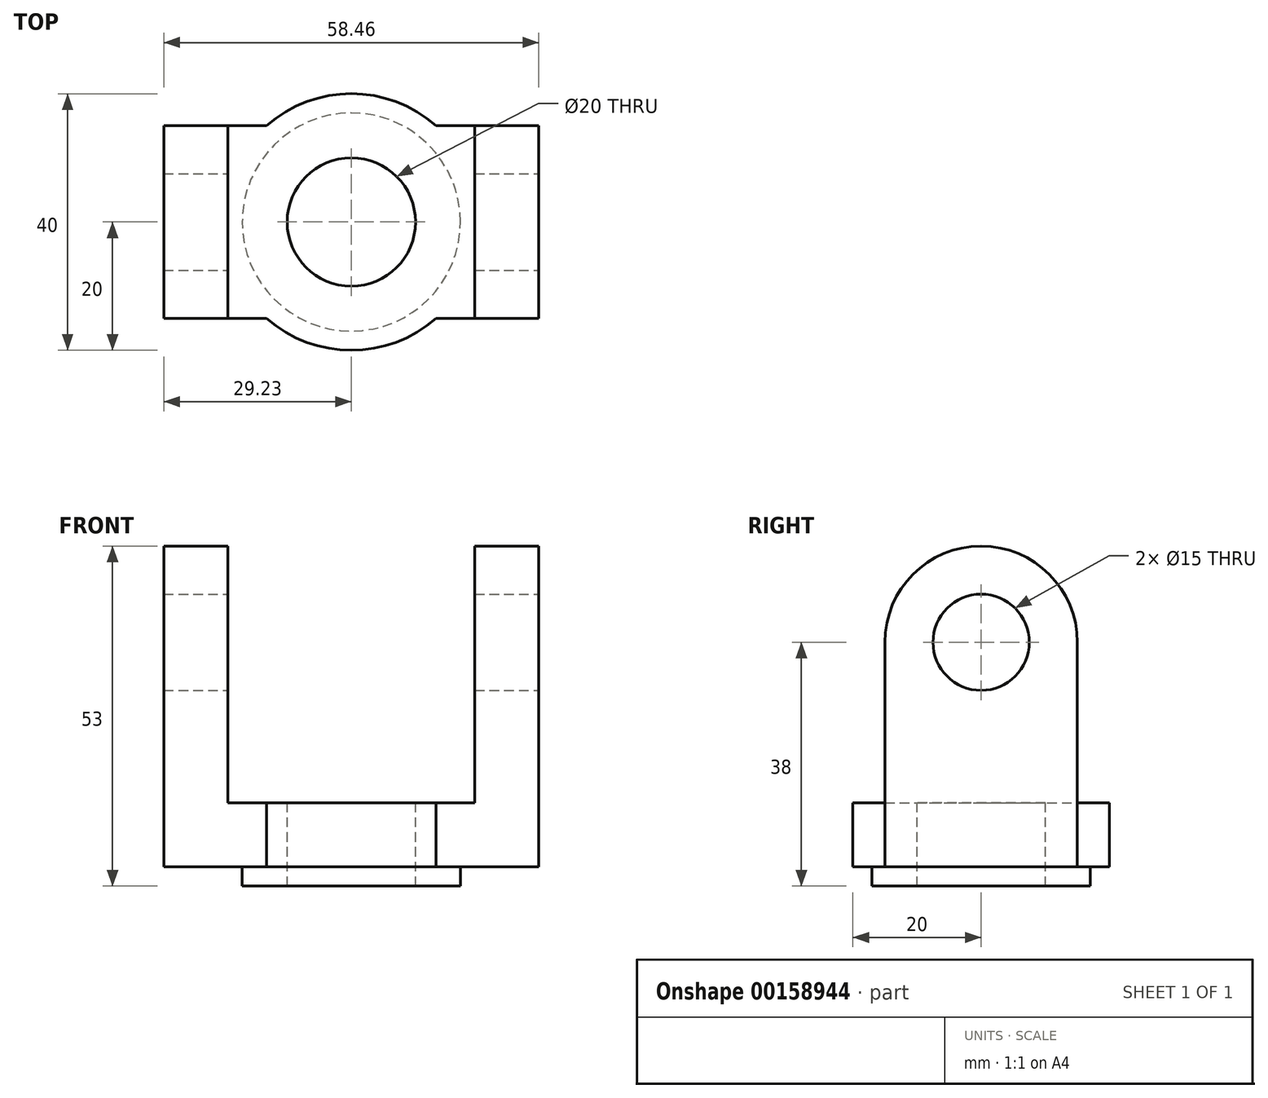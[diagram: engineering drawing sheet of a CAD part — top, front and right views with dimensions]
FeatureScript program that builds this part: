
annotation { "Feature Type Name" : "Feature", "Feature Type Description" : "" }
export const myFeature = defineFeature(function(context is Context, id is Id, definition is map)
    precondition{}
    {
        {
            var Q0;
            Q0=qCreatedBy(makeId("Top.planeOp"),FACE);
            var sketch = newSketch(context, id + "F0", { "sketchPlane" : qUnion([Q0])});
            skLineSegment(sketch, "E0.left", {"start": v(-29.23, -15) * mm, "end": v(-29.23, 15) * mm});
            skLineSegment(sketch, "E0.right", {"start": v(29.23, -15) * mm, "end": v(29.23, 15) * mm});
            skLineSegment(sketch, "E1", {"start": v(-29.23, 15) * mm, "end": v(-13.23, 15) * mm});
            skLineSegment(sketch, "E2", {"start": v(29.23, 15) * mm, "end": v(13.23, 15) * mm});
            skArc(sketch, "E3", {"start": v(13.23, 15) * mm, "mid": v(0, 20) * mm, "end": v(-13.23, 15) * mm});
            skLineSegment(sketch, "E4", {"start": v(-29.23, -15) * mm, "end": v(-13.23, -15) * mm});
            skLineSegment(sketch, "E5", {"start": v(29.23, -15) * mm, "end": v(13.23, -15) * mm});
            skArc(sketch, "E6", {"start": v(-13.23, -15) * mm, "mid": v(0, -20) * mm, "end": v(13.23, -15) * mm});
            skSolve(sketch);
        }
        {
            var Q0;
            Q0=makeQuery(id+"F0.imprint","IMPRINT",FACE,{"disambiguationData":[TD([[makeQuery(id+"F0.imprint","IMPRINT",EDGE,{"derivedFrom":sQuery(id+"F0.wireOp",EDGE,"E0.left")}),-1.0]])]});
            extrude(context, id + "F1", {"entities" : qUnion([Q0]), "depth" : 10 * mm});
        }
        {
            var Q0;
            Q0=makeQuery(id+"F1.opExtrude","SWEPT_FACE",FACE,{"disambiguationData":[OSD([sQuery(id+"F0.wireOp",EDGE,"E0.right")])]});
            var sketch = newSketch(context, id + "F2", { "sketchPlane" : qUnion([Q0])});
            skLineSegment(sketch, "E7", {"start": v(-15, 10) * mm, "end": v(-15, 35) * mm});
            skLineSegment(sketch, "E8", {"start": v(15, 10) * mm, "end": v(15, 35) * mm});
            skLineSegment(sketch, "E9", {"start": v(-15, 10) * mm, "end": v(15, 10) * mm});
            skArc(sketch, "E10", {"start": v(15, 35) * mm, "mid": v(0, 50) * mm, "end": v(-15, 35) * mm});
            skSolve(sketch);
        }
        {
            var Q0;
            Q0 = qSketchRegion(id + "F2", true);
            extrude(context, id + "F3", {"entities" : qUnion([Q0]), "operationType" : NewBodyOperationType.ADD, "oppositeDirection" : true, "depth" : 10 * mm});
        }
        {
            var Q0;
            Q0=makeQuery(id+"F1.opExtrude","SWEPT_FACE",FACE,{"disambiguationData":[OSD([sQuery(id+"F0.wireOp",EDGE,"E0.left")])]});
            var sketch = newSketch(context, id + "F4", { "sketchPlane" : qUnion([Q0])});
            skLineSegment(sketch, "E11", {"start": v(-15, 10) * mm, "end": v(-15, 35) * mm});
            skLineSegment(sketch, "E12", {"start": v(-15, 10) * mm, "end": v(15, 10) * mm});
            skLineSegment(sketch, "E13", {"start": v(15, 10) * mm, "end": v(15, 35) * mm});
            skArc(sketch, "E14", {"start": v(15, 35) * mm, "mid": v(0, 50) * mm, "end": v(-15, 35) * mm});
            skSolve(sketch);
        }
        {
            var Q0;
            Q0 = qSketchRegion(id + "F4", true);
            extrude(context, id + "F5", {"entities" : qUnion([Q0]), "operationType" : NewBodyOperationType.ADD, "oppositeDirection" : true, "depth" : 10 * mm});
        }
        {
            var Q0;
            Q0=makeQuery(id+"F1.opExtrude","CAP_FACE",FACE,{"disambiguationData":[OSD([sQuery(id+"F0.wireOp",EDGE,"E0.left"),sQuery(id+"F0.wireOp",EDGE,"E0.right"),sQuery(id+"F0.wireOp",EDGE,"E1"),sQuery(id+"F0.wireOp",EDGE,"E2"),sQuery(id+"F0.wireOp",EDGE,"E3"),sQuery(id+"F0.wireOp",EDGE,"E4"),sQuery(id+"F0.wireOp",EDGE,"E5"),sQuery(id+"F0.wireOp",EDGE,"E6")])],"isStart":false});
            var sketch = newSketch(context, id + "F6", { "sketchPlane" : qUnion([Q0])});
            skCircle(sketch, "E15", {"center": v(0, 0) * mm, "radius": 10 * mm});
            skSolve(sketch);
        }
        {
            var Q0;
            Q0 = qSketchRegion(id + "F6", true);
            extrude(context, id + "F7", {"entities" : qUnion([Q0]), "operationType" : NewBodyOperationType.REMOVE, "endBound" : BoundingType.THROUGH_ALL, "oppositeDirection" : true, "depth" : 25 * mm});
        }
        {
            var Q0;
            Q0=makeQuery(id+"F1.opExtrude","CAP_FACE",FACE,{"disambiguationData":[OSD([sQuery(id+"F0.wireOp",EDGE,"E0.left"),sQuery(id+"F0.wireOp",EDGE,"E0.right"),sQuery(id+"F0.wireOp",EDGE,"E1"),sQuery(id+"F0.wireOp",EDGE,"E2"),sQuery(id+"F0.wireOp",EDGE,"E3"),sQuery(id+"F0.wireOp",EDGE,"E4"),sQuery(id+"F0.wireOp",EDGE,"E5"),sQuery(id+"F0.wireOp",EDGE,"E6")])],"isStart":true});
            var sketch = newSketch(context, id + "F8", { "sketchPlane" : qUnion([Q0])});
            skCircle(sketch, "E16", {"center": v(0, 0) * mm, "radius": 17 * mm});
            skSolve(sketch);
        }
        {
            var Q0;
            Q0=makeQuery(id+"F8.imprint","IMPRINT",FACE,{"disambiguationData":[TD([[makeQuery(id+"F8.imprint","IMPRINT",EDGE,{"derivedFrom":sQuery(id+"F8.wireOp",EDGE,"E16")}),1.0]])]});
            extrude(context, id + "F9", {"entities" : qUnion([Q0]), "operationType" : NewBodyOperationType.ADD, "depth" : 3 * mm});
        }
        {
            var Q0;
            Q0=makeQuery(id+"F3.boolean.opBoolean","MERGE",FACE,{"derivedFrom":[makeQuery(id+"F1.opExtrude","SWEPT_FACE",FACE,{"disambiguationData":[OSD([sQuery(id+"F0.wireOp",EDGE,"E0.right")])]}),makeQuery(id+"F3.opExtrude","CAP_FACE",FACE,{"disambiguationData":[OSD([sQuery(id+"F2.wireOp",EDGE,"E7"),sQuery(id+"F2.wireOp",EDGE,"E8"),sQuery(id+"F2.wireOp",EDGE,"E9"),sQuery(id+"F2.wireOp",EDGE,"E10")])],"isStart":true})]});
            var sketch = newSketch(context, id + "F10", { "sketchPlane" : qUnion([Q0])});
            skCircle(sketch, "E17", {"center": v(0, 35) * mm, "radius": 7.5 * mm});
            skSolve(sketch);
        }
        {
            var Q0;
            Q0 = qSketchRegion(id + "F10", true);
            extrude(context, id + "F11", {"entities" : qUnion([Q0]), "operationType" : NewBodyOperationType.REMOVE, "endBound" : BoundingType.THROUGH_ALL, "oppositeDirection" : true, "depth" : 25 * mm});
        }
    });
